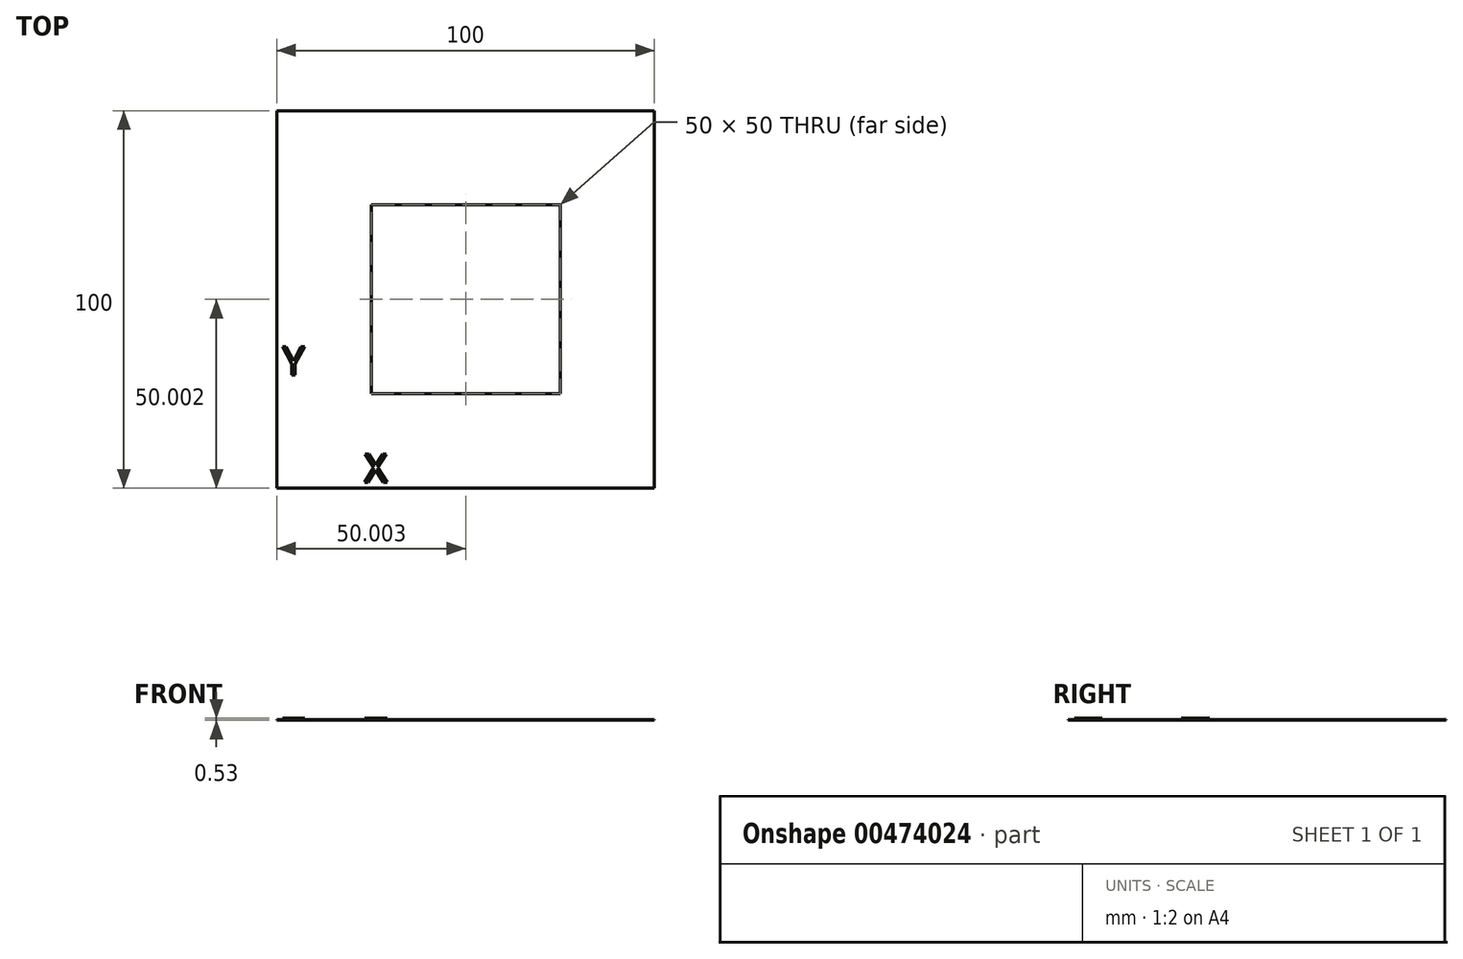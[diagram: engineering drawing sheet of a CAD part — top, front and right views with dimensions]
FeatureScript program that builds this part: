
annotation { "Feature Type Name" : "Feature", "Feature Type Description" : "" }
export const myFeature = defineFeature(function(context is Context, id is Id, definition is map)
    precondition{}
    {
        {
            var Q0;
            Q0=qCreatedBy(makeId("Top.planeOp"),FACE);
            var sketch = newSketch(context, id + "F0", { "sketchPlane" : qUnion([Q0])});
            skLineSegment(sketch, "E0.bottom", {"start": v(-35.72, 42.67) * mm, "end": v(64.28, 42.67) * mm});
            skLineSegment(sketch, "E0.top", {"start": v(-35.72, -57.33) * mm, "end": v(64.28, -57.33) * mm});
            skLineSegment(sketch, "E0.left", {"start": v(-35.72, 42.67) * mm, "end": v(-35.72, -57.33) * mm});
            skLineSegment(sketch, "E0.right", {"start": v(64.28, 42.67) * mm, "end": v(64.28, -57.33) * mm});
            skPoint(sketch, "E1", {"position": v(14.28, -7.33) * mm});
            skLineSegment(sketch, "E2.bottom", {"start": v(-10.72, 17.67) * mm, "end": v(39.28, 17.67) * mm});
            skLineSegment(sketch, "E2.top", {"start": v(-10.72, -32.33) * mm, "end": v(39.28, -32.33) * mm});
            skLineSegment(sketch, "E2.left", {"start": v(-10.72, 17.67) * mm, "end": v(-10.72, -32.33) * mm});
            skLineSegment(sketch, "E2.right", {"start": v(39.28, 17.67) * mm, "end": v(39.28, -32.33) * mm});
            skSolve(sketch);
        }
        {
            var Q0;
            Q0=qSketchRegion(id+"F0",true);
            extrude(context, id + "F1", {"entities" : qUnion([Q0]), "depth" : 0.17 * mm});
        }
        {
            var Q0;
            Q0=makeQuery(id+"F1.opExtrude","CAP_FACE",FACE,{"disambiguationData":[OSD([sQuery(id+"F0.wireOp",EDGE,"E0.bottom"),sQuery(id+"F0.wireOp",EDGE,"E0.top"),sQuery(id+"F0.wireOp",EDGE,"E0.left"),sQuery(id+"F0.wireOp",EDGE,"E0.right")])],"isStart":false});
            var sketch = newSketch(context, id + "F2", { "sketchPlane" : qUnion([Q0])});
            skPoint(sketch, "E3", {"position": v(14.28, -7.33) * mm});
            skText(sketch, "E4", { "text": "Y\n\n        X", "fontName": "OpenSans-Regular.ttf"});
            const initialGuessF2  = {"E4": [-0.03425, -0.02735, 1, 0, 0.00752]};
            skSetInitialGuess(sketch, initialGuessF2);
            skSolve(sketch);
        }
        {
            var Q0;
            Q0=qSketchRegion(id+"F2",true);
            extrude(context, id + "F3", {"entities" : qUnion([Q0]), "operationType" : NewBodyOperationType.ADD, "depth" : .35 * mm});
        }
    });
